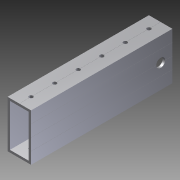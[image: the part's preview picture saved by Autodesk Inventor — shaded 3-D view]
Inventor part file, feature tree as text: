
AUTODESK INVENTOR PART (.ipt)
format: ipt  version: 2014 SP1 (Build 180222100, 222)  size: 693,760 bytes
history: native  units: in
note: dims shown in document units (in); Inventor stores cm internally (conversion verified against a paired STEP export)
features: other x2, extrude x2, sketch x2, imported_body x1
ambient origin geometry x8: Origin, YZ Plane, XZ Plane, XY Plane, X Axis, Y Axis, Z Axis, Center Point
bodies: Body1 (feature_tree)
feature tree (7):
  other  "Cut-Extrude2"
  other  "2x1 Tube1"
  extrude  "Extrusion1"  Depth=0.375in
  extrude  "Extrusion2"  Depth=1.0in TaperAngle=0.0deg
  imported_body  "Base1"
  sketch  "Sketch1"  dims[d0=53.0in d1=0.0in d2=0.375in]
  sketch  "Sketch2"  dims[d3=0.5in d4=1.0in d5=0.0in]
